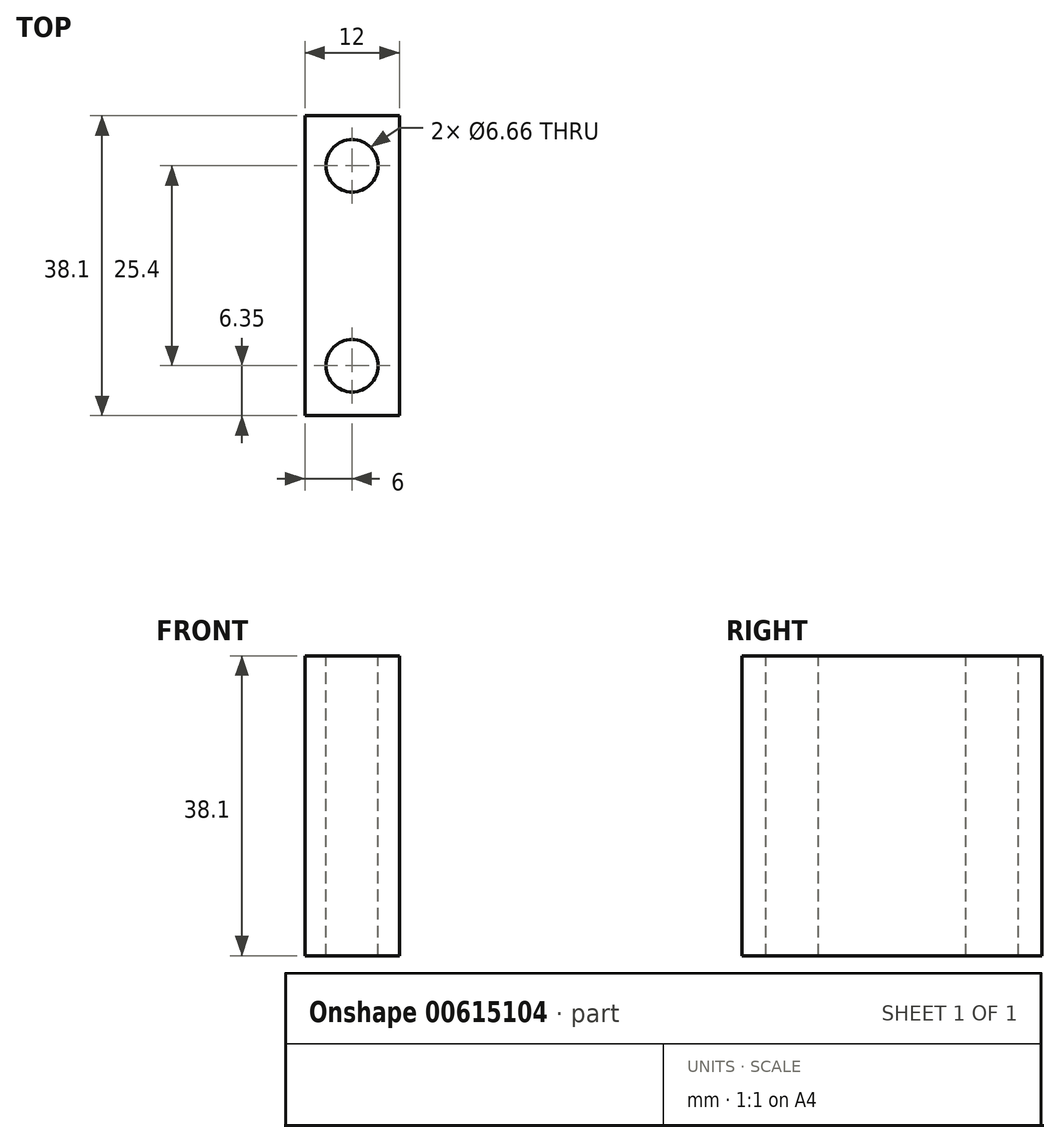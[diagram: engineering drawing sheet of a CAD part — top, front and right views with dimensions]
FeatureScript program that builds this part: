
annotation { "Feature Type Name" : "Feature", "Feature Type Description" : "" }
export const myFeature = defineFeature(function(context is Context, id is Id, definition is map)
    precondition{}
    {
        {
            var Q0;
            Q0=qCreatedBy(makeId("Top.planeOp"),FACE);
            var sketch = newSketch(context, id + "F0", { "sketchPlane" : qUnion([Q0])});
            skLineSegment(sketch, "E0.bottom", {"start": v(6, 19.05) * mm, "end": v(-6, 19.05) * mm});
            skLineSegment(sketch, "E0.top", {"start": v(6, -19.05) * mm, "end": v(-6, -19.05) * mm});
            skLineSegment(sketch, "E0.left", {"start": v(6, 19.05) * mm, "end": v(6, -19.05) * mm});
            skLineSegment(sketch, "E0.right", {"start": v(-6, 19.05) * mm, "end": v(-6, -19.05) * mm});
            skPoint(sketch, "E0.middle", {"position": v(0, 0) * mm});
            skSolve(sketch);
        }
        {
            var Q0;
            Q0 = qSketchRegion(id + "F0", true);
            extrude(context, id + "F1", {"entities" : qUnion([Q0]), "depth" : 38.1 * mm, "offsetDistance" : 25.4 * mm});
        }
        {
            var Q0;
            Q0=makeQuery(id+"F1.opExtrude","CAP_FACE",FACE,{"disambiguationData":[OSD([sQuery(id+"F0.wireOp",EDGE,"E0.bottom"),sQuery(id+"F0.wireOp",EDGE,"E0.top"),sQuery(id+"F0.wireOp",EDGE,"E0.left"),sQuery(id+"F0.wireOp",EDGE,"E0.right")])],"isStart":false});
            var sketch = newSketch(context, id + "F2", { "sketchPlane" : qUnion([Q0])});
            skCircle(sketch, "E1", {"center": v(0, -12.7) * mm, "radius": 3.33 * mm});
            skCircle(sketch, "E2", {"center": v(0, 12.7) * mm, "radius": 3.33 * mm});
            skSolve(sketch);
        }
        {
            var Q0;
            Q0 = qSketchRegion(id + "F2", true);
            extrude(context, id + "F3", {"entities" : qUnion([Q0]), "operationType" : NewBodyOperationType.REMOVE, "endBound" : BoundingType.THROUGH_ALL, "oppositeDirection" : true, "depth" : 25.4 * mm, "offsetDistance" : 25.4 * mm});
        }
    });
